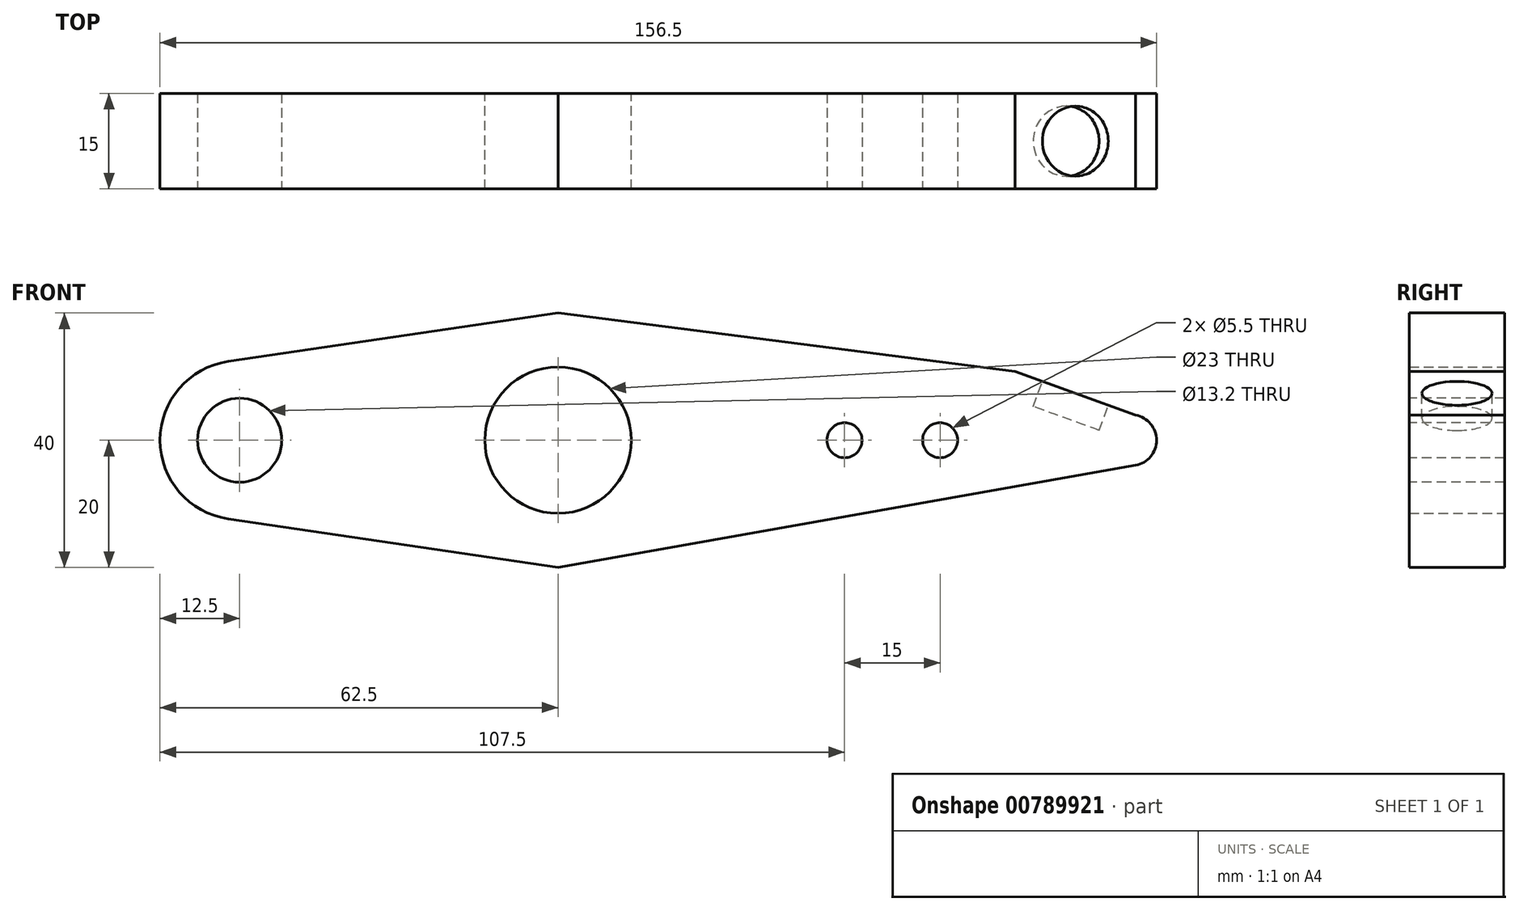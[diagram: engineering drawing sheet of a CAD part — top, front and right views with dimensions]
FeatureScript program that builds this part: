
annotation { "Feature Type Name" : "Feature", "Feature Type Description" : "" }
export const myFeature = defineFeature(function(context is Context, id is Id, definition is map)
    precondition{}
    {
        {
            var Q0;
            Q0=qCreatedBy(makeId("Front.planeOp"),FACE);
            var sketch = newSketch(context, id + "F0", { "sketchPlane" : qUnion([Q0])});
            skCircle(sketch, "E0", {"center": v(0, 0) * mm, "radius": 11.5 * mm});
            skCircle(sketch, "E1", {"center": v(-50, 0) * mm, "radius": 6 * mm, "construction": true});
            skCircle(sketch, "E2", {"center": v(45, 0) * mm, "radius": 2.5 * mm, "construction": true});
            skCircle(sketch, "E3", {"center": v(60, 0) * mm, "radius": 2.5 * mm, "construction": true});
            skLineSegment(sketch, "E4", {"start": v(0, 20) * mm, "end": v(-51.82, 12.37) * mm});
            skArc(sketch, "E5", {"start": v(-51.82, 12.37) * mm, "mid": v(-62.5, 0) * mm, "end": v(-51.82, -12.37) * mm});
            skLineSegment(sketch, "E6", {"start": v(-51.82, -12.37) * mm, "end": v(0, -20) * mm});
            skLineSegment(sketch, "E7", {"start": v(0, -20) * mm, "end": v(90.7, -3.94) * mm});
            skArc(sketch, "E8", {"start": v(90.7, -3.94) * mm, "mid": v(94, 0) * mm, "end": v(90.7, 3.94) * mm});
            skLineSegment(sketch, "E9", {"start": v(90.7, 3.94) * mm, "end": v(71.78, 10.8) * mm});
            skLineSegment(sketch, "E10", {"start": v(71.78, 10.8) * mm, "end": v(0, 20) * mm});
            skLineSegment(sketch, "E11", {"start": v(90.63, -9.98) * mm, "end": v(99.74, 15.11) * mm, "construction": true});
            skPoint(sketch, "E12", {"position": v(81.24, 7.37) * mm});
            skSolve(sketch);
        }
        {
            var Q0;
            Q0=makeQuery(id+"F0.imprint","IMPRINT",FACE,{"disambiguationData":[TD([[makeQuery(id+"F0.imprint","IMPRINT",EDGE,{"derivedFrom":sQuery(id+"F0.wireOp",EDGE,"E0")}),-1.0]])]});
            extrude(context, id + "F1", {"entities" : qUnion([Q0]), "depth" : 15 * mm, "offsetDistance" : 25 * mm});
        }
        {
            var Q0;
            Q0=makeQuery(id+"F1.opExtrude","CAP_FACE",FACE,{"disambiguationData":[OSD([sQuery(id+"F0.wireOp",EDGE,"E0"),sQuery(id+"F0.wireOp",EDGE,"E4"),sQuery(id+"F0.wireOp",EDGE,"E5"),sQuery(id+"F0.wireOp",EDGE,"E6"),sQuery(id+"F0.wireOp",EDGE,"E7"),sQuery(id+"F0.wireOp",EDGE,"E8"),sQuery(id+"F0.wireOp",EDGE,"E9"),sQuery(id+"F0.wireOp",EDGE,"E10")])],"isStart":true});
            var sketch = newSketch(context, id + "F2", { "sketchPlane" : qUnion([Q0])});
            skPoint(sketch, "E13.0", {"position": v(-60, 0) * mm});
            skPoint(sketch, "E14.0", {"position": v(-45, 0) * mm});
            skPoint(sketch, "E15.0", {"position": v(50, 0) * mm});
            skSolve(sketch);
        }
        {
            var Q0;
            Q0=sQuery(id+"F2.wireOp",VERTEX,"E13.0");
            var Q1;
            Q1=sQuery(id+"F2.wireOp",VERTEX,"E14.0");
            var Q2;
            Q2=makeQuery(id+"F1.opExtrude","SWEPT_BODY",BODY,{"disambiguationData":[OSD([sQuery(id+"F0.wireOp",EDGE,"E0"),sQuery(id+"F0.wireOp",EDGE,"E4"),sQuery(id+"F0.wireOp",EDGE,"E5"),sQuery(id+"F0.wireOp",EDGE,"E6"),sQuery(id+"F0.wireOp",EDGE,"E7"),sQuery(id+"F0.wireOp",EDGE,"E8"),sQuery(id+"F0.wireOp",EDGE,"E9"),sQuery(id+"F0.wireOp",EDGE,"E10")])]});
            hole(context, id + "F3", {"style" : HoleStyle.SIMPLE, "endStyle" : HoleEndStyle.THROUGH, "standardTappedOrClearance" : lookupTablePath({ "standard" : "ISO", "fit" : "Normal", "size" : "M5", "type" : "Clearance" }), "standardBlindInLast" : lookupTablePath({ "fit" : "Standard", "standard" : "ISO", "size" : "M5", "type" : "Clearance" }), "holeDiameter" : 5.5 * mm, "majorDiameter" : 5 * mm, "isTappedThrough" : true, "tappedDepth" : 12 * mm, "tapClearance" : 3, "locations" : qUnion([Q0, Q1]), "scope" : qUnion([Q2]), "startStyle" : HoleStartStyle.PART});
        }
        {
            var Q0;
            Q0=sQuery(id+"F0.wireOp",VERTEX,"E1.center");
            var Q1;
            Q1=makeQuery(id+"F1.opExtrude","SWEPT_BODY",BODY,{"disambiguationData":[OSD([sQuery(id+"F0.wireOp",EDGE,"E0"),sQuery(id+"F0.wireOp",EDGE,"E4"),sQuery(id+"F0.wireOp",EDGE,"E5"),sQuery(id+"F0.wireOp",EDGE,"E6"),sQuery(id+"F0.wireOp",EDGE,"E7"),sQuery(id+"F0.wireOp",EDGE,"E8"),sQuery(id+"F0.wireOp",EDGE,"E9"),sQuery(id+"F0.wireOp",EDGE,"E10")])]});
            hole(context, id + "F4", {"style" : HoleStyle.SIMPLE, "endStyle" : HoleEndStyle.THROUGH, "oppositeDirection" : true, "standardTappedOrClearance" : lookupTablePath({ "standard" : "ISO", "fit" : "Normal", "size" : "M12", "type" : "Clearance" }), "standardBlindInLast" : lookupTablePath({ "fit" : "Standard", "standard" : "ISO", "size" : "M12", "type" : "Clearance" }), "holeDiameter" : 13.2 * mm, "majorDiameter" : 5 * mm, "isTappedThrough" : true, "tappedDepth" : 12 * mm, "tapClearance" : 3, "locations" : qUnion([Q0]), "scope" : qUnion([Q1]), "startStyle" : HoleStartStyle.PART});
        }
        {
            var Q0;
            Q0=makeQuery(id+"F1.opExtrude","SWEPT_FACE",FACE,{"disambiguationData":[OSD([sQuery(id+"F0.wireOp",EDGE,"E9")])]});
            var sketch = newSketch(context, id + "F5", { "sketchPlane" : qUnion([Q0])});
            skCircle(sketch, "E16", {"center": v(73.84, -7.5) * mm, "radius": 5.5 * mm});
            skPoint(sketch, "E16.centerSnap0", {"position": v(63.78, -7.5) * mm});
            skPoint(sketch, "E16.centerSnap1", {"position": v(73.84, -15) * mm});
            skSolve(sketch);
        }
        {
            var Q0;
            Q0=makeQuery(id+"F5.imprint","IMPRINT",FACE,{"disambiguationData":[TD([[makeQuery(id+"F5.imprint","IMPRINT",EDGE,{"derivedFrom":sQuery(id+"F5.wireOp",EDGE,"E16")}),1.0]])]});
            extrude(context, id + "F6", {"entities" : qUnion([Q0]), "operationType" : NewBodyOperationType.REMOVE, "oppositeDirection" : true, "depth" : 4.2 * mm, "offsetDistance" : 25 * mm});
        }
    });
